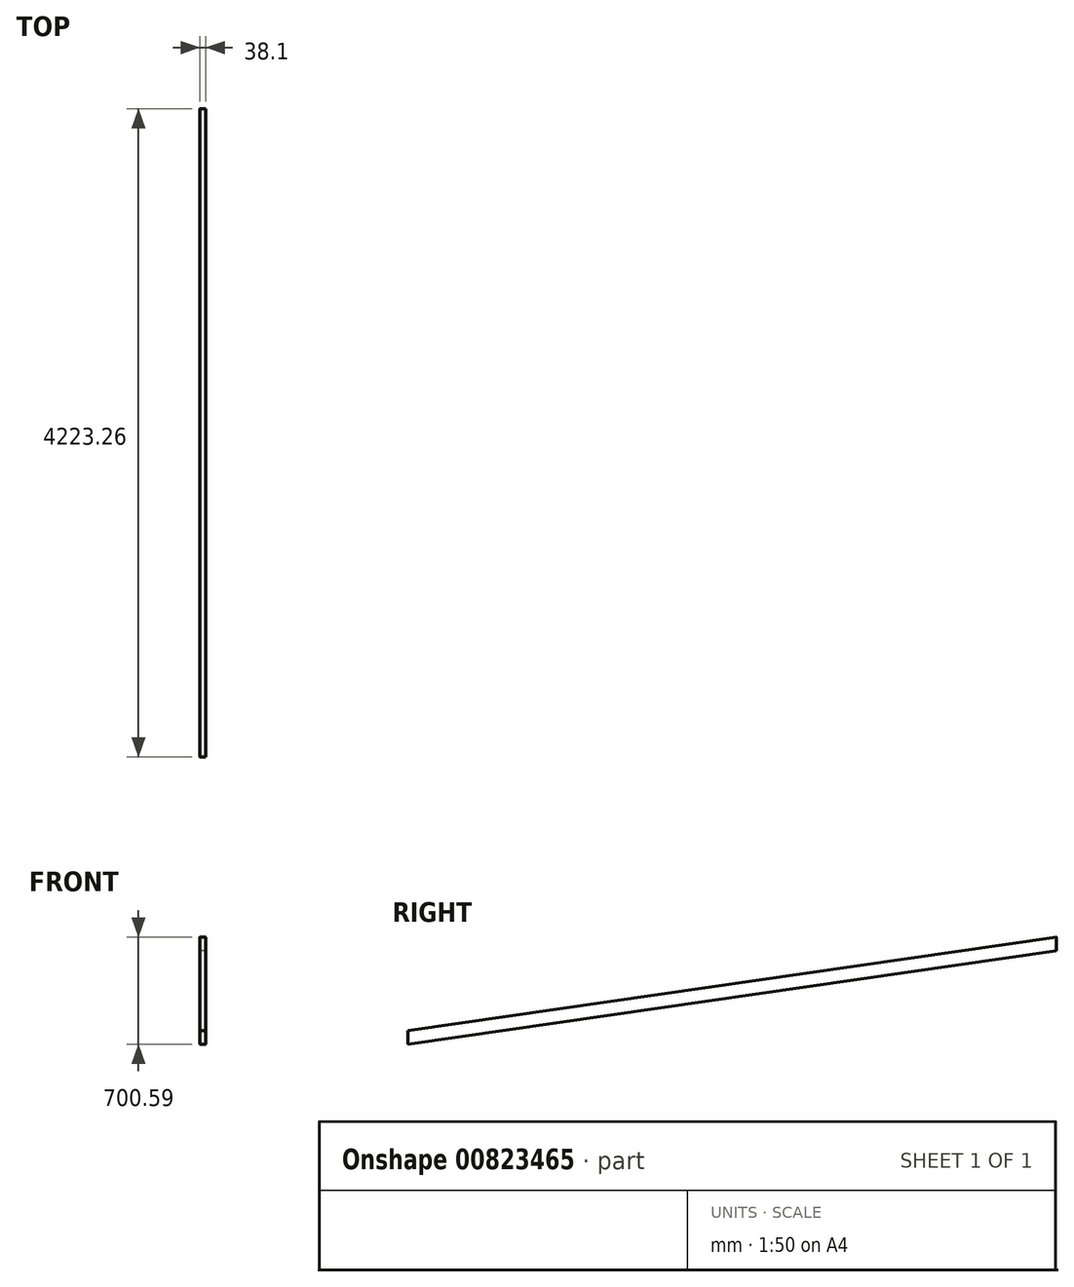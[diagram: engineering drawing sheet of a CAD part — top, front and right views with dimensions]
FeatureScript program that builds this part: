
annotation { "Feature Type Name" : "Feature", "Feature Type Description" : "" }
export const myFeature = defineFeature(function(context is Context, id is Id, definition is map)
    precondition{}
    {
        {
            var Q0;
            Q0=qCreatedBy(makeId("Right.planeOp"),FACE);
            var sketch = newSketch(context, id + "F0", { "sketchPlane" : qUnion([Q0])});
            skLineSegment(sketch, "E0", {"start": v(0, 0) * mm, "end": v(-11.37, 88.9) * mm, "construction": true});
            skLineSegment(sketch, "E1", {"start": v(-11.37, 88.9) * mm, "end": v(-4278.57, 88.9) * mm, "construction": true});
            skLineSegment(sketch, "E2", {"start": v(-4278.57, 88.9) * mm, "end": v(-4216.88, 0) * mm, "construction": true});
            skLineSegment(sketch, "E3", {"start": v(-4216.88, 0) * mm, "end": v(0, 0) * mm, "construction": true});
            skLineSegment(sketch, "E4", {"start": v(-11.37, 88.9) * mm, "end": v(-11.37, -211.84) * mm, "construction": true});
            skLineSegment(sketch, "E5", {"start": v(-11.37, 88.9) * mm, "end": v(-4234.63, -521.86) * mm, "construction": true});
            skLineSegment(sketch, "E6.top", {"start": v(-3605.47, -609.6) * mm, "end": v(-3516.57, -609.6) * mm, "construction": true});
            skLineSegment(sketch, "E6.right", {"start": v(-3516.57, -520.7) * mm, "end": v(-3516.57, -609.6) * mm, "construction": true});
            skPoint(sketch, "E6.middle", {"position": v(-3561.02, -565.15) * mm});
            skLineSegment(sketch, "E7", {"start": v(-11.37, 88.9) * mm, "end": v(-11.37, -0.92) * mm});
            skLineSegment(sketch, "E8", {"start": v(-11.37, -0.92) * mm, "end": v(-4234.63, -611.69) * mm});
            skLineSegment(sketch, "E9", {"start": v(-4234.63, -611.69) * mm, "end": v(-4234.63, -521.86) * mm});
            skLineSegment(sketch, "E10", {"start": v(-11.37, 88.9) * mm, "end": v(-4234.63, -521.86) * mm});
            skLineSegment(sketch, "E11", {"start": v(-3605.47, -609.6) * mm, "end": v(-3605.47, -520.7) * mm, "construction": true});
            skLineSegment(sketch, "E12", {"start": v(-3605.47, -520.7) * mm, "end": v(-3516.57, -520.7) * mm, "construction": true});
            skSolve(sketch);
        }
        {
            var Q0;
            Q0 = qSketchRegion(id + "F0", true);
            extrude(context, id + "F1", {"entities" : qUnion([Q0]), "endBound" : BoundingType.SYMMETRIC, "depth" : 38.1 * mm, "offsetDistance" : 25.4 * mm});
        }
        {
            var Q0;
            Q0=makeQuery(id+"F1.opExtrude","CAP_EDGE",EDGE,{"disambiguationData":[OSD([sQuery(id+"F0.wireOp",EDGE,"E10")])],"isStart":false});
            var Q1;
            Q1=makeQuery(id+"F1.opExtrude","CAP_EDGE",EDGE,{"disambiguationData":[OSD([sQuery(id+"F0.wireOp",EDGE,"E10")])],"isStart":true});
            var Q2;
            Q2=makeQuery(id+"F1.opExtrude","CAP_EDGE",EDGE,{"disambiguationData":[OSD([sQuery(id+"F0.wireOp",EDGE,"E8")])],"isStart":false});
            var Q3;
            Q3=makeQuery(id+"F1.opExtrude","CAP_EDGE",EDGE,{"disambiguationData":[OSD([sQuery(id+"F0.wireOp",EDGE,"E8")])],"isStart":true});
            fillet(context, id + "F2", {"entities" : qUnion([Q0, Q1, Q2, Q3]), "radius" : 5.08 * mm, "tangentPropagation" : true, "allowEdgeOverflow" : false});
        }
    });
